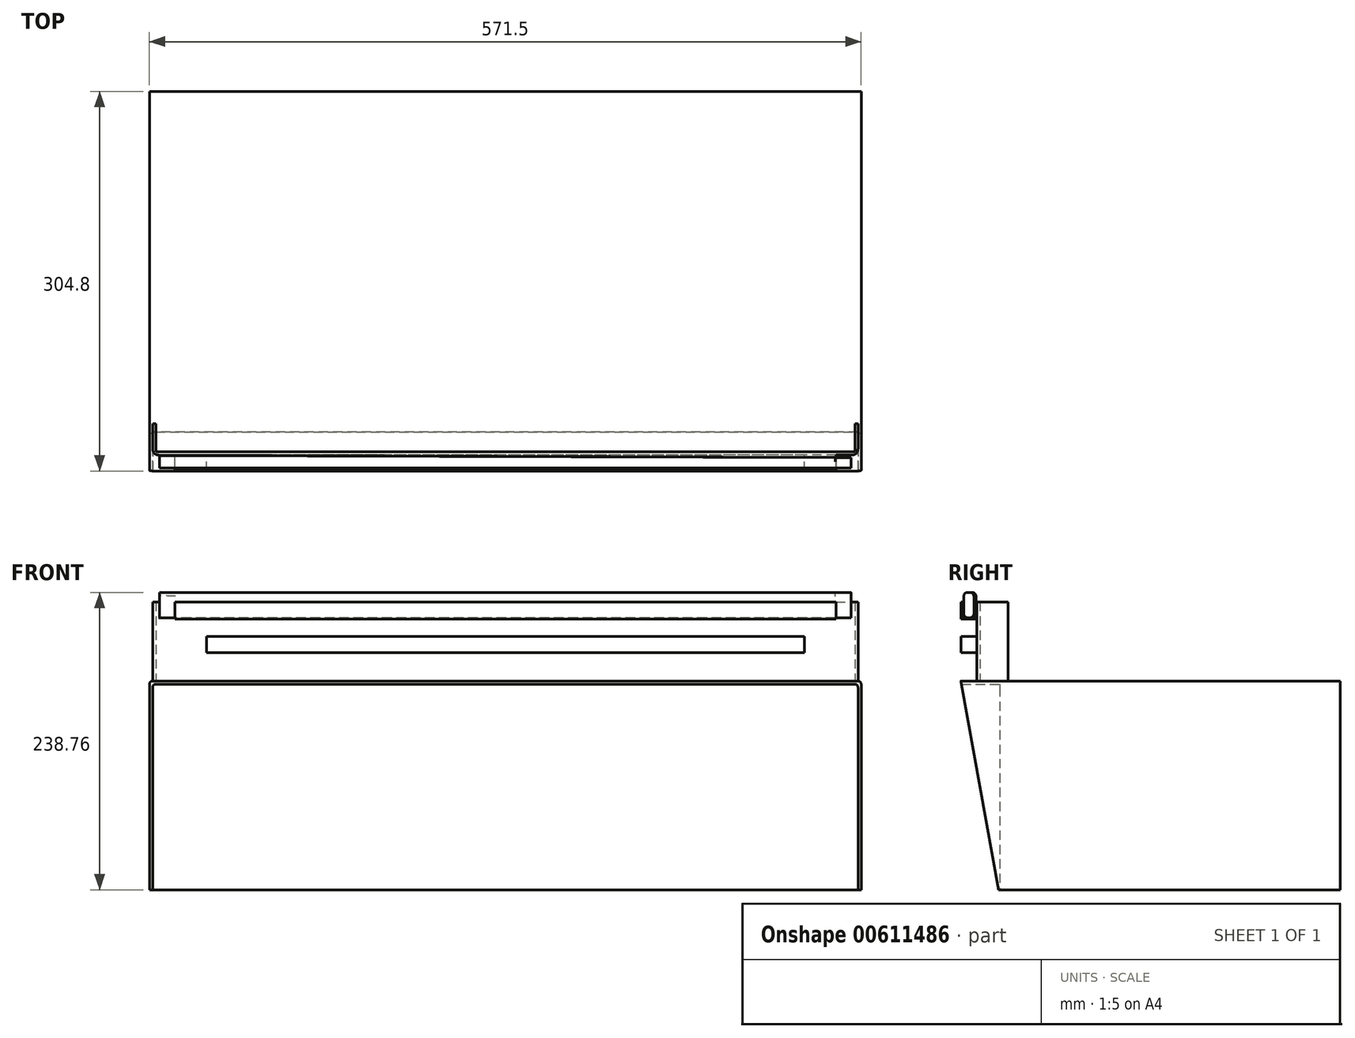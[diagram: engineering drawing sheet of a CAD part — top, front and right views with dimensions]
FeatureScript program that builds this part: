
annotation { "Feature Type Name" : "Feature", "Feature Type Description" : "" }
export const myFeature = defineFeature(function(context is Context, id is Id, definition is map)
    precondition{}
    {
        {
            var Q0;
            Q0=qCreatedBy(makeId("Front.planeOp"),FACE);
            var sketch = newSketch(context, id + "F0", { "sketchPlane" : qUnion([Q0])});
            skLineSegment(sketch, "E0", {"start": v(-1027.16, 0) * mm, "end": v(-455.66, 0) * mm});
            skLineSegment(sketch, "E1", {"start": v(-455.66, 0) * mm, "end": v(-455.66, -167.64) * mm});
            skLineSegment(sketch, "E2", {"start": v(-455.66, -167.64) * mm, "end": v(-1027.16, -167.64) * mm});
            skLineSegment(sketch, "E3", {"start": v(-1027.16, -167.64) * mm, "end": v(-1027.16, 0) * mm});
            skSolve(sketch);
        }
        {
            var Q0;
            Q0=makeQuery(id+"F0.imprint","IMPRINT",FACE,{"disambiguationData":[TD([[makeQuery(id+"F0.imprint","IMPRINT",EDGE,{"derivedFrom":sQuery(id+"F0.wireOp",EDGE,"E0")}),-1.0]])]});
            extrude(context, id + "F1", {"entities" : qUnion([Q0]), "depth" : 304.8 * mm, "offsetDistance" : 25.4 * mm});
        }
        {
            var Q0;
            Q0=makeQuery(id+"F1.opExtrude","SWEPT_FACE",FACE,{"disambiguationData":[OSD([sQuery(id+"F0.wireOp",EDGE,"E1")])]});
            var sketch = newSketch(context, id + "F2", { "sketchPlane" : qUnion([Q0])});
            skLineSegment(sketch, "E4", {"start": v(0, -167.64) * mm, "end": v(-274.32, -167.64) * mm});
            skLineSegment(sketch, "E5", {"start": v(-274.32, -167.64) * mm, "end": v(-304.8, 0) * mm});
            skLineSegment(sketch, "E6", {"start": v(-304.8, 0) * mm, "end": v(-304.8, -167.64) * mm});
            skLineSegment(sketch, "E7", {"start": v(-304.8, -167.64) * mm, "end": v(-274.32, -167.64) * mm});
            skSolve(sketch);
        }
        {
            var Q0;
            Q0 = qSketchRegion(id + "F2", true);
            extrude(context, id + "F3", {"entities" : qUnion([Q0]), "operationType" : NewBodyOperationType.REMOVE, "oppositeDirection" : true, "depth" : 571.5 * mm, "offsetDistance" : 25.4 * mm});
        }
        {
            var Q0;
            Q0=makeQuery(id+"F3.boolean.opBoolean","COPY",FACE,{"derivedFrom":makeQuery(id+"F3.opExtrude","SWEPT_FACE",FACE,{"disambiguationData":[OSD([sQuery(id+"F2.wireOp",EDGE,"E5")])]})});
            shell(context, id + "F4", {"entities" : qUnion([Q0]), "thickness" : 2.54 * mm});
        }
        {
            var Q0;
            Q0=makeQuery(id+"F1.opExtrude","SWEPT_EDGE",EDGE,{"disambiguationData":[OSD([sQuery(id+"F0.wireOp",EDGE,"E0"),sQuery(id+"F0.wireOp",EDGE,"E1")])]});
            var Q1;
            Q1=makeQuery(id+"F1.opExtrude","SWEPT_EDGE",EDGE,{"disambiguationData":[OSD([sQuery(id+"F0.wireOp",EDGE,"E0"),sQuery(id+"F0.wireOp",EDGE,"E3")])]});
            fillet(context, id + "F5", {"entities" : qUnion([Q0, Q1]), "radius" : 2.54 * mm, "tangentPropagation" : true, "allowEdgeOverflow" : false});
        }
        {
            var Q0;
            Q0=makeQuery(id+"F4.opShell","OFFSET_EDGE",EDGE,{"disambiguationData":[OSD([sQuery(id+"F0.wireOp",EDGE,"E0"),sQuery(id+"F0.wireOp",EDGE,"E1")])]});
            fillet(context, id + "F6", {"entities" : qUnion([Q0]), "radius" : 2.54 * mm, "tangentPropagation" : true, "allowEdgeOverflow" : false});
        }
        {
            var Q0;
            Q0=makeQuery(id+"F4.opShell","OFFSET_EDGE",EDGE,{"disambiguationData":[OSD([sQuery(id+"F0.wireOp",EDGE,"E0"),sQuery(id+"F0.wireOp",EDGE,"E3")])]});
            fillet(context, id + "F7", {"entities" : qUnion([Q0]), "radius" : 2.54 * mm, "tangentPropagation" : true, "allowEdgeOverflow" : false});
        }
        {
            var Q0;
            Q0=makeQuery(id+"F1.opExtrude","SWEPT_FACE",FACE,{"disambiguationData":[OSD([sQuery(id+"F0.wireOp",EDGE,"E0")])]});
            var sketch = newSketch(context, id + "F8", { "sketchPlane" : qUnion([Q0])});
            skLineSegment(sketch, "E8", {"start": v(-458.2, -304.8) * mm, "end": v(-458.2, -292.05) * mm});
            skLineSegment(sketch, "E9", {"start": v(-458.2, -292.05) * mm, "end": v(-1024.62, -292.05) * mm});
            skLineSegment(sketch, "E10", {"start": v(-458.2, -292.05) * mm, "end": v(-458.2, -266.7) * mm});
            skLineSegment(sketch, "E11", {"start": v(-458.2, -266.7) * mm, "end": v(-1024.62, -266.7) * mm});
            skLineSegment(sketch, "E12", {"start": v(-1024.62, -266.7) * mm, "end": v(-1024.62, -292.05) * mm});
            skSolve(sketch);
        }
        {
            var Q0;
            Q0=makeQuery(id+"F8.imprint","IMPRINT",FACE,{"disambiguationData":[TD([[makeQuery(id+"F8.imprint","IMPRINT",EDGE,{"derivedFrom":sQuery(id+"F8.wireOp",EDGE,"E9")}),-1.0]])]});
            extrude(context, id + "F9", {"entities" : qUnion([Q0]), "operationType" : NewBodyOperationType.ADD, "depth" : 63.5 * mm, "offsetDistance" : 25.4 * mm});
        }
        {
            var Q0;
            Q0=makeQuery(id+"F9.opExtrude","SWEPT_FACE",FACE,{"disambiguationData":[OSD([sQuery(id+"F8.wireOp",EDGE,"E11")])]});
            shell(context, id + "F10", {"entities" : qUnion([Q0]), "thickness" : 2.54 * mm});
        }
        {
            var Q0;
            Q0=makeQuery(id+"F9.opExtrude","SWEPT_EDGE",EDGE,{"disambiguationData":[OSD([sQuery(id+"F8.wireOp",EDGE,"E8"),sQuery(id+"F8.wireOp",EDGE,"E9"),sQuery(id+"F8.wireOp",EDGE,"E10")])]});
            var Q1;
            Q1=makeQuery(id+"F9.opExtrude","SWEPT_EDGE",EDGE,{"disambiguationData":[OSD([sQuery(id+"F0.wireOp",EDGE,"E0"),sQuery(id+"F0.wireOp",EDGE,"E3"),sQuery(id+"F8.wireOp",EDGE,"E9"),sQuery(id+"F8.wireOp",EDGE,"E12")])]});
            fillet(context, id + "F11", {"entities" : qUnion([Q0, Q1]), "radius" : 5.08 * mm, "tangentPropagation" : true, "allowEdgeOverflow" : false});
        }
        {
            var Q0;
            Q0=makeQuery(id+"F4.opShell","OFFSET_FACE",FACE,{"disambiguationData":[OSD([sQuery(id+"F0.wireOp",EDGE,"E2")])]});
            var sketch = newSketch(context, id + "F12", { "sketchPlane" : qUnion([Q0])});
            skLineSegment(sketch, "E13", {"start": v(-1024.62, -274.78) * mm, "end": v(-1024.62, -251.94) * mm});
            skLineSegment(sketch, "E14", {"start": v(-1024.62, -251.94) * mm, "end": v(-458.2, -251.94) * mm});
            skLineSegment(sketch, "E15", {"start": v(-458.2, -251.94) * mm, "end": v(-458.2, -2.54) * mm});
            skLineSegment(sketch, "E16", {"start": v(-458.2, -2.54) * mm, "end": v(-1024.62, -2.54) * mm});
            skLineSegment(sketch, "E17", {"start": v(-1024.62, -2.54) * mm, "end": v(-1024.62, -251.94) * mm});
            skSolve(sketch);
        }
        {
            var Q0;
            Q0 = qSketchRegion(id + "F12", true);
            extrude(context, id + "F13", {"entities" : qUnion([Q0]), "operationType" : NewBodyOperationType.ADD, "depth" : 162.56 * mm, "offsetDistance" : 25.4 * mm});
        }
        {
            var Q0;
            Q0=makeQuery(id+"F4.opShell","OFFSET_FACE",FACE,{"disambiguationData":[OSD([sQuery(id+"F0.wireOp",EDGE,"E2")])]});
            extrude(context, id + "F14", {"entities" : qUnion([Q0]), "operationType" : NewBodyOperationType.REMOVE, "oppositeDirection" : true, "depth" : 25.4 * mm, "offsetDistance" : 25.4 * mm});
        }
        {
            var Q0;
            {var subQ0=sQuery(id+"F12.wireOp",EDGE,"E14");Q0=makeQuery(id+"F14.boolean.opBoolean","MERGE",FACE,{"derivedFrom":[makeQuery(id+"F13.opExtrude","SWEPT_FACE",FACE,{"disambiguationData":[OSD([subQ0])]}),makeQuery(id+"F14.opExtrude","SWEPT_FACE",FACE,{"disambiguationData":[OSD([subQ0])]})]});}
            extrude(context, id + "F15", {"entities" : qUnion([Q0]), "operationType" : NewBodyOperationType.ADD, "depth" : 21.59 * mm, "offsetDistance" : 25.4 * mm});
        }
        {
            var Q0;
            Q0=makeQuery(id+"F9.opExtrude","SWEPT_FACE",FACE,{"disambiguationData":[OSD([sQuery(id+"F8.wireOp",EDGE,"E9")])]});
            var sketch = newSketch(context, id + "F16", { "sketchPlane" : qUnion([Q0])});
            skLineSegment(sketch, "E18", {"start": v(-463.28, 0) * mm, "end": v(-463.28, 22.83) * mm});
            skLineSegment(sketch, "E19", {"start": v(-463.28, 22.83) * mm, "end": v(-1019.54, 22.83) * mm});
            skLineSegment(sketch, "E20", {"start": v(-1019.54, 22.83) * mm, "end": v(-1019.54, 0) * mm});
            skLineSegment(sketch, "E21", {"start": v(-1019.54, 0) * mm, "end": v(-463.28, 0) * mm});
            skLineSegment(sketch, "E22", {"start": v(-463.28, 22.83) * mm, "end": v(-463.28, 35.78) * mm});
            skLineSegment(sketch, "E23", {"start": v(-463.28, 35.78) * mm, "end": v(-1019.54, 35.78) * mm});
            skLineSegment(sketch, "E24", {"start": v(-1019.54, 35.78) * mm, "end": v(-1019.54, 22.83) * mm});
            skSolve(sketch);
        }
        {
            var Q0;
            Q0=makeQuery(id+"F16.imprint","IMPRINT",FACE,{"disambiguationData":[TD([[makeQuery(id+"F16.imprint","IMPRINT",EDGE,{"derivedFrom":sQuery(id+"F16.wireOp",EDGE,"E19")}),-1.0]])]});
            extrude(context, id + "F17", {"entities" : qUnion([Q0]), "operationType" : NewBodyOperationType.ADD, "depth" : 12.7 * mm, "offsetDistance" : 25.4 * mm});
        }
        {
            var Q0;
            {var subQ1=sQuery(id+"F8.wireOp",EDGE,"E9");Q0=makeQuery(id+"F17.boolean.opBoolean","SPLIT",FACE,{"disambiguationData":[TD([makeQuery(id+"F17.opExtrude","SWEPT_FACE",FACE,{"disambiguationData":[OSD([sQuery(id+"F16.wireOp",EDGE,"E23")])]})])],"derivedFrom":makeQuery(id+"F9.opExtrude","SWEPT_FACE",FACE,{"disambiguationData":[OSD([subQ1])]})});}
            var sketch = newSketch(context, id + "F18", { "sketchPlane" : qUnion([Q0])});
            skLineSegment(sketch, "E25", {"start": v(-463.28, 35.78) * mm, "end": v(-463.28, 49.64) * mm});
            skLineSegment(sketch, "E26", {"start": v(-463.28, 49.64) * mm, "end": v(-1019.54, 49.64) * mm});
            skLineSegment(sketch, "E27", {"start": v(-1019.54, 49.64) * mm, "end": v(-1019.54, 63.5) * mm});
            skLineSegment(sketch, "E28", {"start": v(-1019.54, 63.5) * mm, "end": v(-463.28, 63.5) * mm});
            skLineSegment(sketch, "E29", {"start": v(-463.28, 63.5) * mm, "end": v(-463.28, 49.64) * mm});
            skSolve(sketch);
        }
        {
            var Q0;
            Q0=makeQuery(id+"F9.opExtrude","CAP_FACE",FACE,{"disambiguationData":[OSD([sQuery(id+"F8.wireOp",EDGE,"E9"),sQuery(id+"F8.wireOp",EDGE,"E10"),sQuery(id+"F8.wireOp",EDGE,"E11"),sQuery(id+"F8.wireOp",EDGE,"E12")])],"isStart":false});
            var sketch = newSketch(context, id + "F19", { "sketchPlane" : qUnion([Q0])});
            skLineSegment(sketch, "E30", {"start": v(-458.2, -266.7) * mm, "end": v(-458.2, -292.05) * mm});
            skLineSegment(sketch, "E31", {"start": v(-458.2, -292.05) * mm, "end": v(-1024.62, -292.05) * mm});
            skLineSegment(sketch, "E32", {"start": v(-1024.62, -292.05) * mm, "end": v(-1024.62, -266.7) * mm});
            skLineSegment(sketch, "E33", {"start": v(-1024.62, -266.7) * mm, "end": v(-458.2, -266.7) * mm});
            skLineSegment(sketch, "E34.0", {"start": v(-460.74, -266.7) * mm, "end": v(-460.74, -289.51) * mm});
            skLineSegment(sketch, "E34.2", {"start": v(-1022.08, -289.51) * mm, "end": v(-1022.08, -266.7) * mm});
            skLineSegment(sketch, "E34.3", {"start": v(-460.74, -289.51) * mm, "end": v(-1022.08, -289.51) * mm});
            skSolve(sketch);
        }
        {
            var Q0;
            {var subQ0=sQuery(id+"F19.wireOp",EDGE,"E34.0");Q0=makeQuery(id+"F19.imprint","IMPRINT",FACE,{"disambiguationData":[TD([[makeQuery(id+"F19.imprint","IMPRINT",EDGE,{"derivedFrom":subQ0}),-1.0]])]});}
            extrude(context, id + "F20", {"entities" : qUnion([Q0]), "operationType" : NewBodyOperationType.REMOVE, "oppositeDirection" : true, "depth" : 25.4 * mm, "offsetDistance" : 25.4 * mm});
        }
        {
            var Q0;
            Q0=makeQuery(id+"F18.imprint","IMPRINT",FACE,{"disambiguationData":[TD([[makeQuery(id+"F18.imprint","IMPRINT",EDGE,{"derivedFrom":sQuery(id+"F18.wireOp",EDGE,"E26")}),-1.0]])]});
            extrude(context, id + "F21", {"entities" : qUnion([Q0]), "operationType" : NewBodyOperationType.ADD, "depth" : 12.7 * mm, "offsetDistance" : 25.4 * mm});
        }
        {
            var Q0;
            Q0=makeQuery(id+"F21.boolean.opBoolean","MERGE",FACE,{"derivedFrom":[makeQuery(id+"F9.opExtrude","CAP_FACE",FACE,{"disambiguationData":[OSD([sQuery(id+"F8.wireOp",EDGE,"E9"),sQuery(id+"F8.wireOp",EDGE,"E10"),sQuery(id+"F8.wireOp",EDGE,"E11"),sQuery(id+"F8.wireOp",EDGE,"E12")])],"isStart":false}),makeQuery(id+"F21.opExtrude","SWEPT_FACE",FACE,{"disambiguationData":[OSD([sQuery(id+"F18.wireOp",EDGE,"E28")])]})]});
            var sketch = newSketch(context, id + "F22", { "sketchPlane" : qUnion([Q0])});
            skLineSegment(sketch, "E35", {"start": v(-463.28, -292.05) * mm, "end": v(-1019.54, -292.05) * mm});
            skLineSegment(sketch, "E36", {"start": v(-1019.54, -292.05) * mm, "end": v(-1019.54, -304.75) * mm});
            skLineSegment(sketch, "E37", {"start": v(-1019.54, -304.75) * mm, "end": v(-463.28, -304.75) * mm});
            skLineSegment(sketch, "E38", {"start": v(-463.28, -304.75) * mm, "end": v(-463.28, -292.05) * mm});
            skLineSegment(sketch, "E39", {"start": v(-463.28, -292.05) * mm, "end": v(-463.28, -293.84) * mm});
            skLineSegment(sketch, "E40", {"start": v(-463.28, -293.84) * mm, "end": v(-1019.54, -292.05) * mm});
            skLineSegment(sketch, "E41", {"start": v(-1019.54, -304.75) * mm, "end": v(-1019.54, -302.98) * mm});
            skLineSegment(sketch, "E42", {"start": v(-1019.54, -302.98) * mm, "end": v(-463.28, -302.98) * mm});
            skLineSegment(sketch, "E43", {"start": v(-463.28, -302.98) * mm, "end": v(-463.28, -293.84) * mm});
            skLineSegment(sketch, "E44", {"start": v(-1019.54, -292.05) * mm, "end": v(-1019.54, -302.98) * mm});
            skSolve(sketch);
        }
        {
            var Q0;
            Q0=makeQuery(id+"F22.imprint","IMPRINT",FACE,{"disambiguationData":[TD([[makeQuery(id+"F22.imprint","IMPRINT",EDGE,{"derivedFrom":sQuery(id+"F22.wireOp",EDGE,"E40")}),1.0]])]});
            extrude(context, id + "F23", {"entities" : qUnion([Q0]), "operationType" : NewBodyOperationType.REMOVE, "oppositeDirection" : true, "depth" : 12.7 * mm, "offsetDistance" : 25.4 * mm});
        }
        {
            var Q0;
            Q0=makeQuery(id+"F17.opExtrude","SWEPT_FACE",FACE,{"disambiguationData":[OSD([sQuery(id+"F16.wireOp",EDGE,"E22")])]});
            extrude(context, id + "F24", {"entities" : qUnion([Q0]), "operationType" : NewBodyOperationType.ADD, "oppositeDirection" : true, "depth" : 25.4 * mm, "offsetDistance" : 25.4 * mm});
        }
        {
            var Q0;
            Q0=makeQuery(id+"F17.opExtrude","SWEPT_FACE",FACE,{"disambiguationData":[OSD([sQuery(id+"F16.wireOp",EDGE,"E22")])]});
            extrude(context, id + "F25", {"entities" : qUnion([Q0]), "operationType" : NewBodyOperationType.ADD, "oppositeDirection" : true, "depth" : 38.1 * mm, "offsetDistance" : 25.4 * mm});
        }
        {
            var Q0;
            Q0=makeQuery(id+"F17.opExtrude","SWEPT_FACE",FACE,{"disambiguationData":[OSD([sQuery(id+"F16.wireOp",EDGE,"E22")])]});
            extrude(context, id + "F26", {"entities" : qUnion([Q0]), "operationType" : NewBodyOperationType.REMOVE, "oppositeDirection" : true, "depth" : 38.1 * mm, "offsetDistance" : 25.4 * mm});
        }
        {
            var Q0;
            Q0=makeQuery(id+"F17.opExtrude","SWEPT_FACE",FACE,{"disambiguationData":[OSD([sQuery(id+"F16.wireOp",EDGE,"E24")])]});
            extrude(context, id + "F27", {"entities" : qUnion([Q0]), "operationType" : NewBodyOperationType.REMOVE, "oppositeDirection" : true, "depth" : 38.1 * mm, "offsetDistance" : 25.4 * mm});
        }
        {
            var Q0;
            Q0=makeQuery(id+"F21.opExtrude","SWEPT_FACE",FACE,{"disambiguationData":[OSD([sQuery(id+"F18.wireOp",EDGE,"E29")])]});
            extrude(context, id + "F28", {"entities" : qUnion([Q0]), "operationType" : NewBodyOperationType.REMOVE, "oppositeDirection" : true, "depth" : 12.7 * mm, "offsetDistance" : 25.4 * mm});
        }
        {
            var Q0;
            Q0=makeQuery(id+"F21.opExtrude","SWEPT_FACE",FACE,{"disambiguationData":[OSD([sQuery(id+"F18.wireOp",EDGE,"E27")])]});
            extrude(context, id + "F29", {"entities" : qUnion([Q0]), "operationType" : NewBodyOperationType.REMOVE, "oppositeDirection" : true, "depth" : 12.7 * mm, "offsetDistance" : 25.4 * mm});
        }
        {
            var Q0;
            Q0=makeQuery(id+"F23.boolean.opBoolean","COPY",FACE,{"derivedFrom":makeQuery(id+"F23.opExtrude","CAP_FACE",FACE,{"disambiguationData":[OSD([sQuery(id+"F22.wireOp",EDGE,"E40"),sQuery(id+"F22.wireOp",EDGE,"E42"),sQuery(id+"F22.wireOp",EDGE,"E43"),sQuery(id+"F22.wireOp",EDGE,"E44")])],"isStart":false})});
            var sketch = newSketch(context, id + "F30", { "sketchPlane" : qUnion([Q0])});
            skLineSegment(sketch, "E45.bottom", {"start": v(-475.98, -293.8) * mm, "end": v(-475.98, -293.8) * mm});
            skLineSegment(sketch, "E45.top", {"start": v(-475.98, -302.98) * mm, "end": v(-475.98, -302.98) * mm});
            skLineSegment(sketch, "E45.left", {"start": v(-475.98, -293.8) * mm, "end": v(-475.98, -302.98) * mm});
            skLineSegment(sketch, "E45.right", {"start": v(-475.98, -293.8) * mm, "end": v(-475.98, -302.98) * mm});
            skLineSegment(sketch, "E46.bottom", {"start": v(-475.98, -302.98) * mm, "end": v(-1006.84, -302.98) * mm});
            skLineSegment(sketch, "E46.top", {"start": v(-475.98, -292.1) * mm, "end": v(-1006.84, -292.1) * mm});
            skLineSegment(sketch, "E46.left", {"start": v(-475.98, -302.98) * mm, "end": v(-475.98, -292.1) * mm});
            skLineSegment(sketch, "E46.right", {"start": v(-1006.84, -302.98) * mm, "end": v(-1006.84, -292.1) * mm});
            skLineSegment(sketch, "E47.0", {"start": v(-476.49, -293.8) * mm, "end": v(-476.49, -302.98) * mm});
            skLineSegment(sketch, "E48.0", {"start": v(-475.98, -302.47) * mm, "end": v(-1006.84, -302.47) * mm});
            skLineSegment(sketch, "E49.0", {"start": v(-1006.33, -302.98) * mm, "end": v(-1006.33, -292.1) * mm});
            skLineSegment(sketch, "E50.0", {"start": v(-475.98, -294.3) * mm, "end": v(-1006.84, -292.6) * mm});
            skSolve(sketch);
        }
        {
            var Q0;
            {var subQ0=sQuery(id+"F30.wireOp",EDGE,"E50.0");var subQ1=sQuery(id+"F30.wireOp",EDGE,"E47.0");var subQ2=makeQuery(id+"F30.imprint","INTERSECT",VERTEX,{"derivedFrom":[subQ1,subQ0]});Q0=makeQuery(id+"F30.imprint","IMPRINT",FACE,{"disambiguationData":[TD([[makeQuery(id+"F30.imprint","IMPRINT",EDGE,{"disambiguationData":[TD([[subQ2,-1.0]])],"derivedFrom":subQ1}),-1.0]])]});}
            extrude(context, id + "F31", {"entities" : qUnion([Q0]), "operationType" : NewBodyOperationType.ADD, "depth" : 20.32 * mm, "offsetDistance" : 25.4 * mm});
        }
        {
            var Q0;
            Q0=makeQuery(id+"F31.opExtrude","SWEPT_FACE",FACE,{"disambiguationData":[OSD([sQuery(id+"F30.wireOp",EDGE,"E49.0")])]});
            extrude(context, id + "F32", {"entities" : qUnion([Q0]), "operationType" : NewBodyOperationType.ADD, "depth" : 12.7 * mm, "offsetDistance" : 25.4 * mm});
        }
        {
            var Q0;
            Q0=makeQuery(id+"F31.opExtrude","SWEPT_FACE",FACE,{"disambiguationData":[OSD([sQuery(id+"F30.wireOp",EDGE,"E47.0")])]});
            extrude(context, id + "F33", {"entities" : qUnion([Q0]), "operationType" : NewBodyOperationType.ADD, "depth" : 12.7 * mm, "offsetDistance" : 25.4 * mm});
        }
        {
            var Q0;
            {var subQ0=sQuery(id+"F30.wireOp",EDGE,"E48.0");var subQ1=sQuery(id+"F30.wireOp",EDGE,"E47.0");var subQ2=sQuery(id+"F30.wireOp",EDGE,"E49.0");Q0=makeQuery(id+"F33.boolean.opBoolean","MERGE",EDGE,{"derivedFrom":[makeQuery(id+"F32.boolean.opBoolean","MERGE",EDGE,{"derivedFrom":[makeQuery(id+"F31.opExtrude","CAP_EDGE",EDGE,{"disambiguationData":[OSD([subQ0])],"isStart":false}),makeQuery(id+"F32.opExtrude","SWEPT_EDGE",EDGE,{"disambiguationData":[OSD([subQ0,subQ2]),TDD([makeQuery(id+"F31.opExtrude","CAP_VERTEX",VERTEX,{"disambiguationData":[OSD([subQ0,subQ2])],"isStart":false})])]})]}),makeQuery(id+"F33.opExtrude","SWEPT_EDGE",EDGE,{"disambiguationData":[OSD([subQ1,subQ0]),TDD([makeQuery(id+"F31.opExtrude","CAP_VERTEX",VERTEX,{"disambiguationData":[OSD([subQ1,subQ0])],"isStart":false})])]})]});}
            var Q1;
            {var subQ0=sQuery(id+"F30.wireOp",EDGE,"E50.0");var subQ1=sQuery(id+"F30.wireOp",EDGE,"E47.0");Q1=makeQuery(id+"F33.opExtrude","SWEPT_EDGE",EDGE,{"disambiguationData":[OSD([subQ1,subQ0]),TDD([makeQuery(id+"F31.opExtrude","CAP_VERTEX",VERTEX,{"disambiguationData":[OSD([subQ1,subQ0])],"isStart":false})])]});}
            var Q2;
            {var subQ0=sQuery(id+"F30.wireOp",EDGE,"E48.0");var subQ1=sQuery(id+"F30.wireOp",EDGE,"E47.0");Q2=makeQuery(id+"F33.boolean.opBoolean","SPLIT",EDGE,{"derivedFrom":makeQuery(id+"F33.opExtrude","SWEPT_EDGE",EDGE,{"disambiguationData":[OSD([subQ1,subQ0]),TDD([makeQuery(id+"F31.opExtrude","CAP_VERTEX",VERTEX,{"disambiguationData":[OSD([subQ1,subQ0])],"isStart":true})])]})});}
            var Q3;
            {var subQ0=sQuery(id+"F30.wireOp",EDGE,"E50.0");var subQ1=sQuery(id+"F30.wireOp",EDGE,"E47.0");Q3=makeQuery(id+"F33.boolean.opBoolean","SPLIT",EDGE,{"disambiguationData":[topologyDisambiguationEdgeConnected([makeQuery(id+"F33.opExtrude","SWEPT_FACE",FACE,{"disambiguationData":[OSD([subQ1]),TDD([makeQuery(id+"F31.opExtrude","CAP_EDGE",EDGE,{"disambiguationData":[OSD([subQ1])],"isStart":true})])]})])],"derivedFrom":makeQuery(id+"F33.opExtrude","SWEPT_EDGE",EDGE,{"disambiguationData":[OSD([subQ1,subQ0]),TDD([makeQuery(id+"F31.opExtrude","CAP_VERTEX",VERTEX,{"disambiguationData":[OSD([subQ1,subQ0])],"isStart":true})])]})});}
            var Q4;
            {var subQ0=sQuery(id+"F30.wireOp",EDGE,"E49.0");var subQ1=sQuery(id+"F30.wireOp",EDGE,"E48.0");Q4=makeQuery(id+"F32.boolean.opBoolean","SPLIT",EDGE,{"derivedFrom":makeQuery(id+"F32.opExtrude","SWEPT_EDGE",EDGE,{"disambiguationData":[OSD([subQ1,subQ0]),TDD([makeQuery(id+"F31.opExtrude","CAP_VERTEX",VERTEX,{"disambiguationData":[OSD([subQ1,subQ0])],"isStart":true})])]})});}
            fillet(context, id + "F34", {"entities" : qUnion([Q0, Q1, Q2, Q3, Q4]), "radius" : 3.17 * mm, "tangentPropagation" : true, "allowEdgeOverflow" : false});
        }
    });
